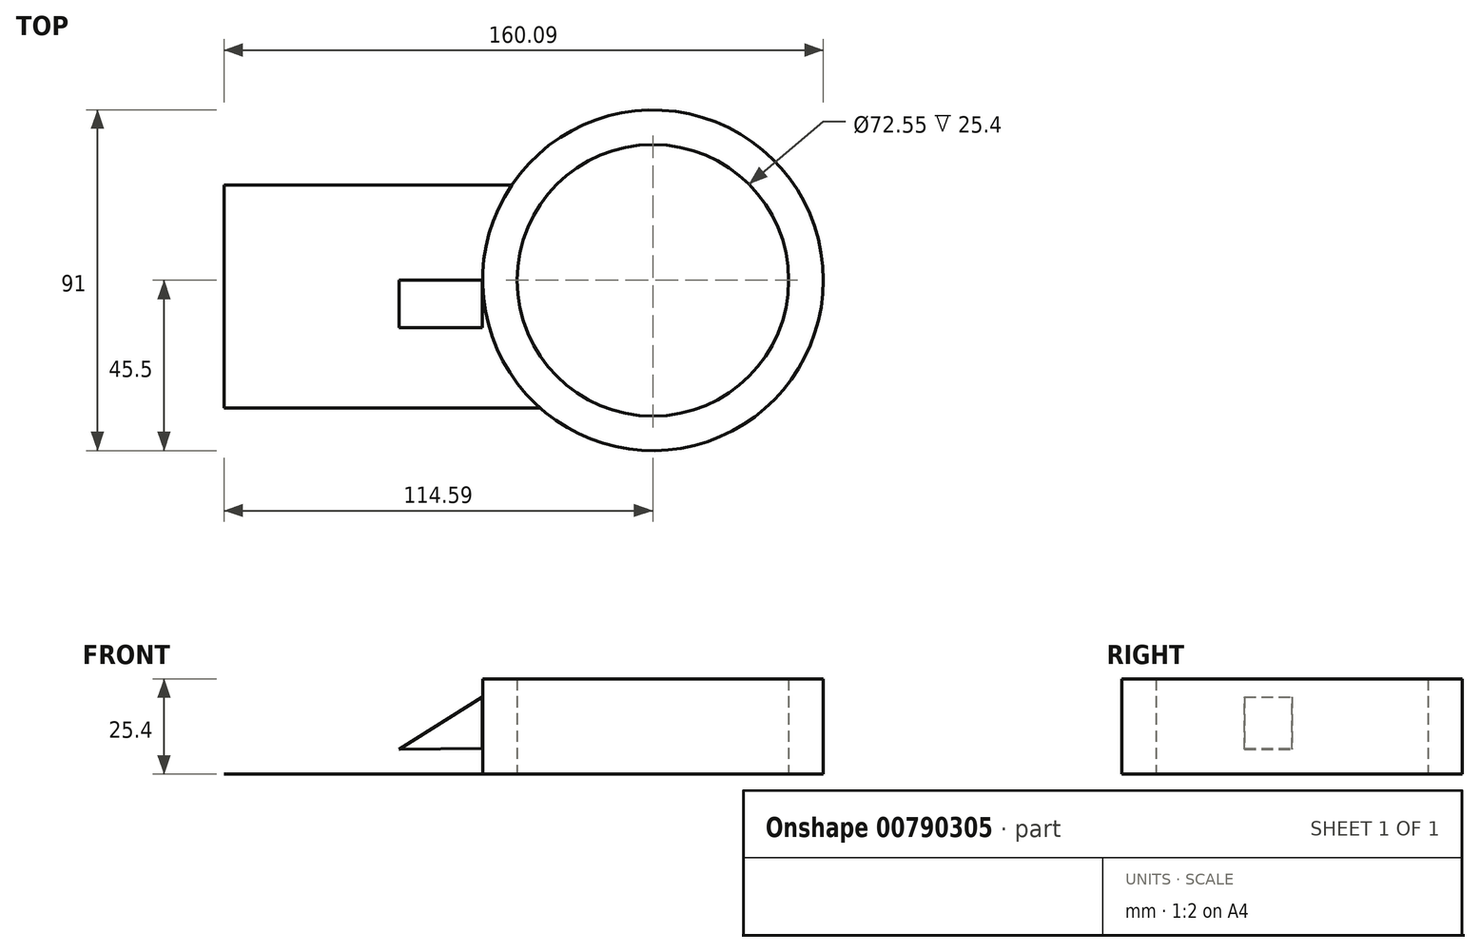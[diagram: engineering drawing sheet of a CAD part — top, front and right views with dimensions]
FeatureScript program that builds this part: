
annotation { "Feature Type Name" : "Feature", "Feature Type Description" : "" }
export const myFeature = defineFeature(function(context is Context, id is Id, definition is map)
    precondition{}
    {
        {
            var Q0;
            Q0=qCreatedBy(makeId("Top.planeOp"),FACE);
            var sketch = newSketch(context, id + "F0", { "sketchPlane" : qUnion([Q0])});
            skCircle(sketch, "E0", {"center": v(0, 0) * mm, "radius": 36.27 * mm});
            skCircle(sketch, "E1", {"center": v(0, 0) * mm, "radius": 45.5 * mm});
            skLineSegment(sketch, "E2.bottom", {"start": v(-114.6, 25.42) * mm, "end": v(-37.73, 25.42) * mm});
            skLineSegment(sketch, "E2.top", {"start": v(-114.6, -34.1) * mm, "end": v(-30.12, -34.1) * mm});
            skLineSegment(sketch, "E2.left", {"start": v(-114.6, 25.42) * mm, "end": v(-114.6, -34.1) * mm});
            skSolve(sketch);
        }
        {
            var Q0;
            Q0=makeQuery(id+"F0.imprint","IMPRINT",FACE,{"disambiguationData":[TD([[makeQuery(id+"F0.imprint","IMPRINT",EDGE,{"derivedFrom":sQuery(id+"F0.wireOp",EDGE,"E0")}),-1.0]])]});
            extrude(context, id + "F1", {"entities" : qUnion([Q0]), "depth" : 25.4 * mm, "offsetDistance" : 25.4 * mm});
        }
        {
            var Q0;
            {var subQ0=sQuery(id+"F0.wireOp",EDGE,"E2.bottom");Q0=makeQuery(id+"F0.imprint","IMPRINT",FACE,{"disambiguationData":[TD([[makeQuery(id+"F0.imprint","IMPRINT",EDGE,{"derivedFrom":subQ0}),-1.0]])]});}
            extrude(context, id + "F2", {"entities" : qUnion([Q0]), "operationType" : NewBodyOperationType.ADD, "depth" : 1 / 101.6 * mm, "offsetDistance" : 25.4 * mm});
        }
        {
            var Q0;
            Q0=qCreatedBy(makeId("Front.planeOp"),FACE);
            var sketch = newSketch(context, id + "F3", { "sketchPlane" : qUnion([Q0])});
            skLineSegment(sketch, "E3", {"start": v(-67.76, 6.63) * mm, "end": v(-45.59, 20.6) * mm});
            skLineSegment(sketch, "E4", {"start": v(-45.59, 20.6) * mm, "end": v(-45.59, 6.87) * mm});
            skLineSegment(sketch, "E5", {"start": v(-45.59, 6.87) * mm, "end": v(-67.76, 6.63) * mm});
            skSolve(sketch);
        }
        {
            var Q0;
            Q0=makeQuery(id+"F3.imprint","IMPRINT",FACE,{"disambiguationData":[TD([[makeQuery(id+"F3.imprint","IMPRINT",EDGE,{"derivedFrom":sQuery(id+"F3.wireOp",EDGE,"E3")}),-1.0]])]});
            extrude(context, id + "F4", {"entities" : qUnion([Q0]), "depth" : 12.7 * mm, "offsetDistance" : 25.4 * mm});
        }
    });
